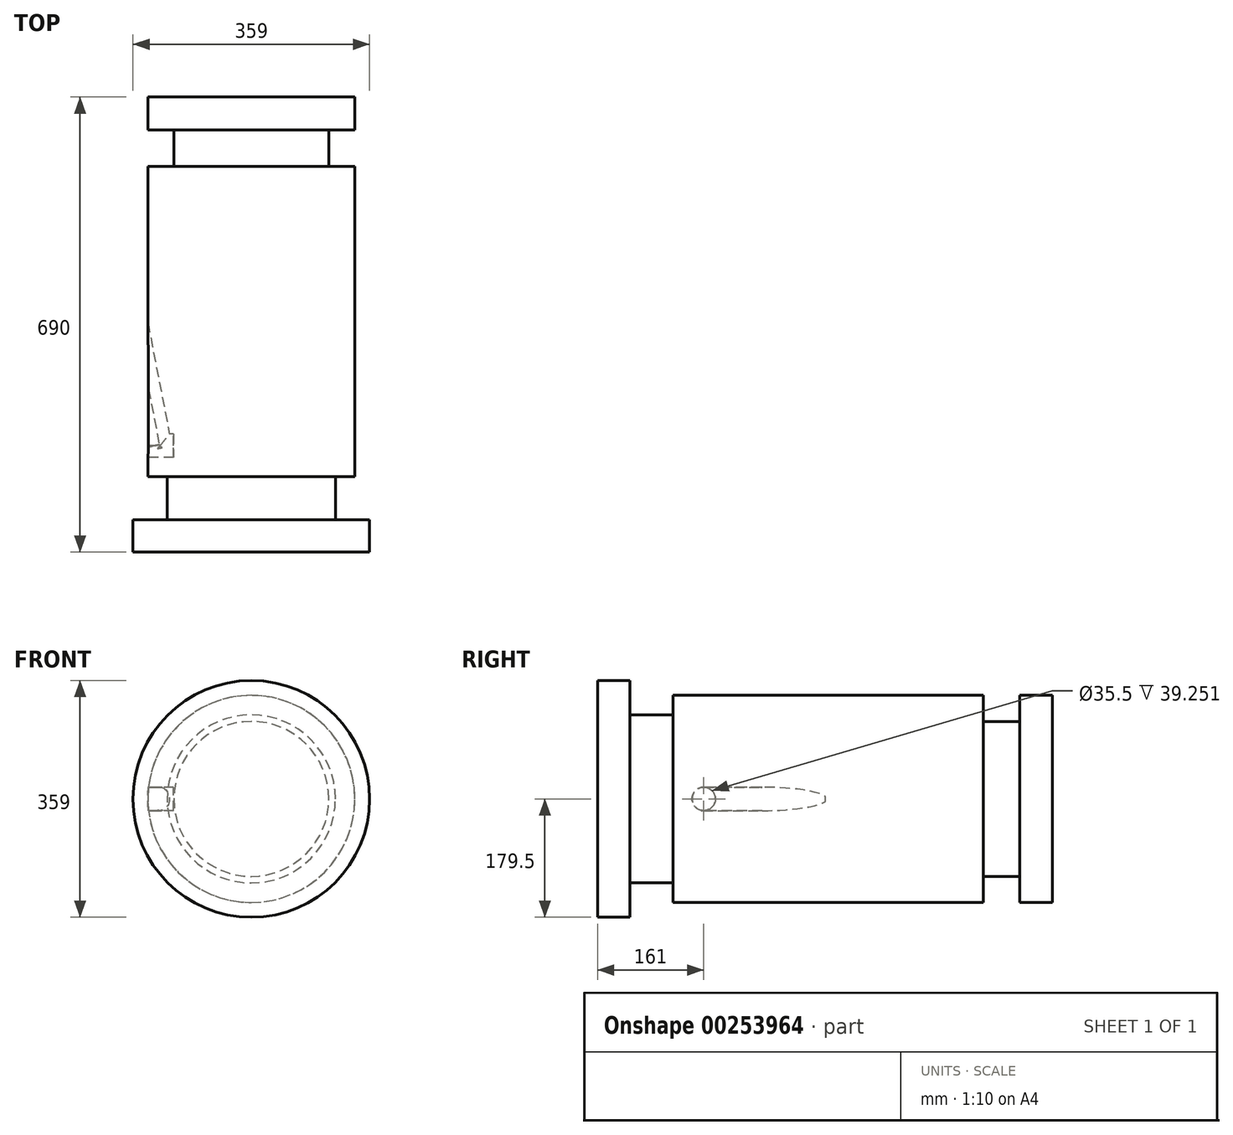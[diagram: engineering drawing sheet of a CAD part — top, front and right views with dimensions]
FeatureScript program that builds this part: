
annotation { "Feature Type Name" : "Feature", "Feature Type Description" : "" }
export const myFeature = defineFeature(function(context is Context, id is Id, definition is map)
    precondition{}
    {
        {
            var Q0;
            Q0=qCreatedBy(makeId("Front.planeOp"),FACE);
            var sketch = newSketch(context, id + "F0", { "sketchPlane" : qUnion([Q0])});
            skCircle(sketch, "E0", {"center": v(0, 0) * mm, "radius": 157 * mm});
            skSolve(sketch);
        }
        {
            var Q0;
            Q0 = qSketchRegion(id + "F0", true);
            extrude(context, id + "F1", {"entities" : qUnion([Q0]), "depth" : 640 * mm});
        }
        {
            var Q0;
            Q0=makeQuery(id+"F1.opExtrude","CAP_FACE",FACE,{"disambiguationData":[OSD([sQuery(id+"F0.wireOp",EDGE,"E0")])],"isStart":false});
            var sketch = newSketch(context, id + "F2", { "sketchPlane" : qUnion([Q0])});
            skCircle(sketch, "E1", {"center": v(0, 0) * mm, "radius": 179.5 * mm});
            skSolve(sketch);
        }
        {
            var Q0;
            Q0 = qSketchRegion(id + "F2", true);
            extrude(context, id + "F3", {"entities" : qUnion([Q0]), "operationType" : NewBodyOperationType.ADD, "depth" : 50 * mm});
        }
        {
            var Q0;
            Q0=qCreatedBy(makeId("Right.planeOp"),FACE);
            var sketch = newSketch(context, id + "F4", { "sketchPlane" : qUnion([Q0])});
            skLineSegment(sketch, "E2", {"start": v(-50, 175.93) * mm, "end": v(-50, 117.5) * mm});
            skLineSegment(sketch, "E3", {"start": v(-50, 117.5) * mm, "end": v(-105, 117.5) * mm});
            skLineSegment(sketch, "E4", {"start": v(-105, 117.5) * mm, "end": v(-105, 176.54) * mm});
            skLineSegment(sketch, "E5", {"start": v(-105, 176.54) * mm, "end": v(-50, 175.93) * mm});
            skLineSegment(sketch, "E6", {"start": v(0, 0) * mm, "end": v(-695.66, 0) * mm});
            skLineSegment(sketch, "E7", {"start": v(-575.86, 204.09) * mm, "end": v(-575.86, 127.5) * mm});
            skLineSegment(sketch, "E8", {"start": v(-575.86, 127.5) * mm, "end": v(-640.86, 127.5) * mm});
            skLineSegment(sketch, "E9", {"start": v(-640.86, 127.5) * mm, "end": v(-640.86, 217.2) * mm});
            skLineSegment(sketch, "E10", {"start": v(-640.86, 217.2) * mm, "end": v(-575.86, 204.09) * mm});
            skSolve(sketch);
        }
        {
            var Q0;
            Q0=makeQuery(id+"F4.imprint","IMPRINT",FACE,{"disambiguationData":[TD([[makeQuery(id+"F4.imprint","IMPRINT",EDGE,{"derivedFrom":sQuery(id+"F4.wireOp",EDGE,"E2")}),-1.0]])]});
            var Q1;
            Q1=makeQuery(id+"F4.imprint","IMPRINT",FACE,{"disambiguationData":[TD([[makeQuery(id+"F4.imprint","IMPRINT",EDGE,{"derivedFrom":sQuery(id+"F4.wireOp",EDGE,"E7")}),-1.0]])]});
            var Q2;
            Q2=sQuery(id+"F4.wireOp",EDGE,"E6");
            revolve(context, id + "F5", {"operationType" : NewBodyOperationType.REMOVE, "entities" : qUnion([Q0, Q1]), "axis" : qUnion([Q2]), "revolveType" : RevolveType.FULL, "oppositeDirection" : true});
        }
        {
            var Q0;
            Q0=qCreatedBy(makeId("Right.planeOp"),FACE);
            cPlane(context, id + "F6", {"entities" : qUnion([Q0]), "cplaneType" : CPlaneType.OFFSET, "offset" : (314 / 2) * mm, "oppositeDirection" : true, "width" : 150 * mm, "height" : 150 * mm});
        }
        {
            var Q0;
            Q0=qCreatedBy(id+"F6.planeOp",FACE);
            var sketch = newSketch(context, id + "F7", { "sketchPlane" : qUnion([Q0])});
            skCircle(sketch, "E11", {"center": v(-529, 0) * mm, "radius": 17.75 * mm});
            skSolve(sketch);
        }
        {
            var Q0;
            Q0 = qSketchRegion(id + "F7", true);
            extrude(context, id + "F8", {"entities" : qUnion([Q0]), "operationType" : NewBodyOperationType.REMOVE, "depth" : (314 / 2 - 117.75) * mm});
        }
        {
            var Q0;
            Q0=qCreatedBy(makeId("Top.planeOp"),FACE);
            var sketch = newSketch(context, id + "F9", { "sketchPlane" : qUnion([Q0])});
            skLineSegment(sketch, "E12", {"start": v(0, 0) * mm, "end": v(0, -700.89) * mm});
            skLineSegment(sketch, "E13", {"start": v(-203.86, -529) * mm, "end": v(-175.42, -529) * mm});
            skLineSegment(sketch, "E14", {"start": v(-120.67, -425.72) * mm, "end": v(-120.67, -529) * mm});
            skLineSegment(sketch, "E15", {"start": v(-175.42, -529) * mm, "end": v(-65.18, -529) * mm});
            skLineSegment(sketch, "E16", {"start": v(-120.67, -529) * mm, "end": v(-171.41, -267.96) * mm});
            skLineSegment(sketch, "E17.0", {"start": v(-138.1, -532.39) * mm, "end": v(-188.84, -271.35) * mm});
            skLineSegment(sketch, "E18", {"start": v(-188.84, -271.35) * mm, "end": v(-171.41, -267.96) * mm});
            skLineSegment(sketch, "E19", {"start": v(-138.1, -532.39) * mm, "end": v(-120.67, -529) * mm});
            skSolve(sketch);
        }
        {
            var Q0;
            {var subQ0=sQuery(id+"F9.wireOp",EDGE,"E16");Q0=makeQuery(id+"F9.imprint","IMPRINT",FACE,{"disambiguationData":[TD([[makeQuery(id+"F9.imprint","IMPRINT",EDGE,{"derivedFrom":subQ0}),1.0]])]});}
            var Q1;
            Q1=sQuery(id+"F9.wireOp",EDGE,"E17.0");
            revolve(context, id + "F10", {"operationType" : NewBodyOperationType.REMOVE, "entities" : qUnion([Q0]), "axis" : qUnion([Q1]), "revolveType" : RevolveType.FULL});
        }
        {
            var Q0;
            Q0=makeQuery(id+"F1.opExtrude","CAP_FACE",FACE,{"disambiguationData":[OSD([sQuery(id+"F0.wireOp",EDGE,"E0")])],"isStart":true});
            var sketch = newSketch(context, id + "F11", { "sketchPlane" : qUnion([Q0])});
            skLineSegment(sketch, "E20", {"start": v(220.07, 245.72) * mm, "end": v(220.07, -455.57) * mm});
            skSolve(sketch);
        }
        {
            var Q0;
            Q0=sQuery(id+"F11.wireOp",EDGE,"E20");
            cPlane(context, id + "F12", {"entities" : qUnion([Q0]), "cplaneType" : CPlaneType.LINE_ANGLE, "offset" : 25 * mm, "angle" : 79 * degree, "width" : 150 * mm, "height" : 150 * mm});
        }
        {
            var Q0;
            Q0=qCreatedBy(id+"F12.planeOp",FACE);
            cPlane(context, id + "F13", {"entities" : qUnion([Q0]), "cplaneType" : CPlaneType.OFFSET, "offset" : 533 * mm, "oppositeDirection" : true, "width" : 150 * mm, "height" : 150 * mm});
        }
        {
            var Q0;
            Q0=qCreatedBy(id+"F13.planeOp",FACE);
            var sketch = newSketch(context, id + "F14", { "sketchPlane" : qUnion([Q0])});
            skArc(sketch, "E21", {"start": v(237.58, 17.75) * mm, "mid": v(219.5, 0.17) * mm, "end": v(237.24, -17.75) * mm});
            skLineSegment(sketch, "E22", {"start": v(237.24, -17.75) * mm, "end": v(285.38, -17.75) * mm});
            skLineSegment(sketch, "E23", {"start": v(285.38, -17.75) * mm, "end": v(285.38, 17.75) * mm});
            skLineSegment(sketch, "E24", {"start": v(236.9, 17.75) * mm, "end": v(285.38, 17.75) * mm});
            skSolve(sketch);
        }
        {
            var Q0;
            Q0 = qSketchRegion(id + "F14", true);
            extrude(context, id + "F15", {"entities" : qUnion([Q0]), "operationType" : NewBodyOperationType.REMOVE, "depth" : 237.6 * mm});
        }
    });
